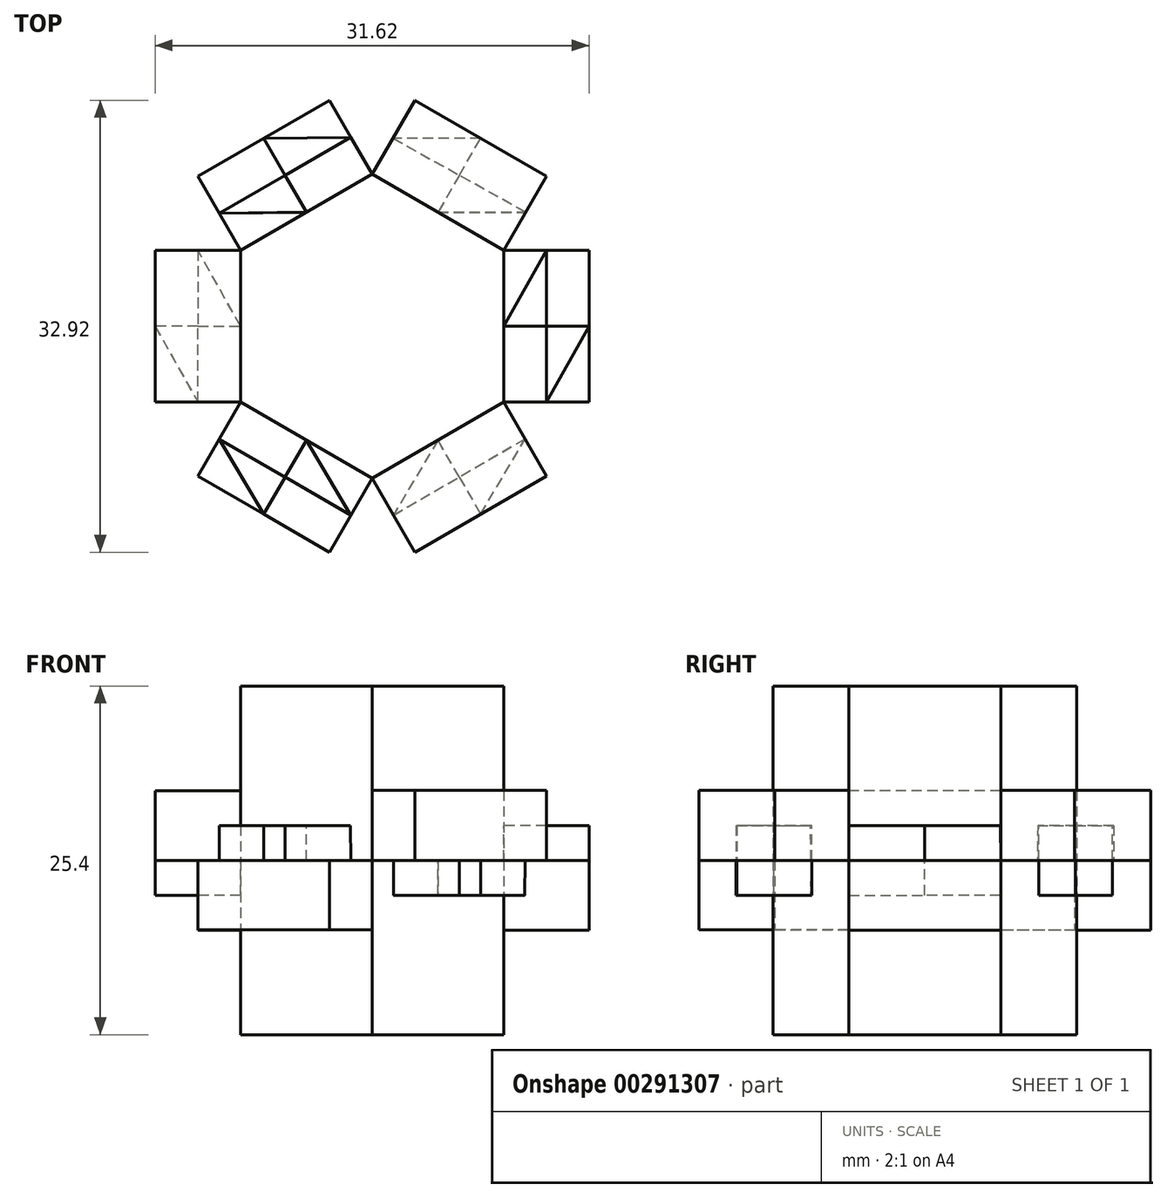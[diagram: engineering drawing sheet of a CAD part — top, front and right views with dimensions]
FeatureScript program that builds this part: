
annotation { "Feature Type Name" : "Feature", "Feature Type Description" : "" }
export const myFeature = defineFeature(function(context is Context, id is Id, definition is map)
    precondition{}
    {
        {
            var Q0;
            Q0=qCreatedBy(makeId("Top.planeOp"),FACE);
            var sketch = newSketch(context, id + "F0", { "sketchPlane" : qUnion([Q0])});
            skCircle(sketch, "E0.cCircle", {"center": v(0, 0) * mm, "radius": 11.07 * mm, "construction": true});
            skLineSegment(sketch, "E0.0", {"start": v(0, 11.07) * mm, "end": v(9.59, 5.53) * mm});
            skLineSegment(sketch, "E0.1", {"start": v(9.59, 5.53) * mm, "end": v(9.59, -5.53) * mm});
            skLineSegment(sketch, "E0.2", {"start": v(9.59, -5.53) * mm, "end": v(0, -11.07) * mm});
            skLineSegment(sketch, "E0.3", {"start": v(0, -11.07) * mm, "end": v(-9.59, -5.53) * mm});
            skLineSegment(sketch, "E0.4", {"start": v(-9.59, -5.53) * mm, "end": v(-9.59, 5.53) * mm});
            skLineSegment(sketch, "E0.5", {"start": v(-9.59, 5.53) * mm, "end": v(0, 11.07) * mm});
            skSolve(sketch);
        }
        {
            var Q0;
            Q0 = qSketchRegion(id + "F0", true);
            extrude(context, id + "F1", {"entities" : qUnion([Q0]), "endBound" : BoundingType.SYMMETRIC, "depth" : 25.4 * mm});
        }
        {
            var Q0;
            Q0=makeQuery(id+"F1.opExtrude","SWEPT_FACE",FACE,{"disambiguationData":[OSD([sQuery(id+"F0.wireOp",EDGE,"E0.4")])]});
            var sketch = newSketch(context, id + "F2", { "sketchPlane" : qUnion([Q0])});
            skLineSegment(sketch, "E1.bottom", {"start": v(-5.53, 0) * mm, "end": v(5.53, 0) * mm});
            skLineSegment(sketch, "E1.top", {"start": v(-5.53, 5.07) * mm, "end": v(5.53, 5.07) * mm});
            skLineSegment(sketch, "E1.left", {"start": v(-5.53, 0) * mm, "end": v(-5.53, 5.07) * mm});
            skLineSegment(sketch, "E1.right", {"start": v(5.53, 0) * mm, "end": v(5.53, 5.07) * mm});
            skSolve(sketch);
        }
        {
            var Q0;
            Q0=makeQuery(id+"F2.imprint","IMPRINT",FACE,{"disambiguationData":[TD([[makeQuery(id+"F2.imprint","IMPRINT",EDGE,{"derivedFrom":sQuery(id+"F2.wireOp",EDGE,"E1.bottom")}),1.0]])]});
            extrude(context, id + "F3", {"entities" : qUnion([Q0]), "operationType" : NewBodyOperationType.ADD, "depth" : 6.22 * mm});
        }
        {
            var Q0;
            Q0=makeQuery(id+"F3.opExtrude","SWEPT_FACE",FACE,{"disambiguationData":[OSD([sQuery(id+"F2.wireOp",EDGE,"E1.bottom")])]});
            var sketch = newSketch(context, id + "F4", { "sketchPlane" : qUnion([Q0])});
            skLineSegment(sketch, "E2", {"start": v(-15.8, 0) * mm, "end": v(-9.59, 0) * mm});
            skLineSegment(sketch, "E3", {"start": v(-9.59, 0) * mm, "end": v(-12.7, -5.53) * mm});
            skLineSegment(sketch, "E4", {"start": v(-12.7, -5.53) * mm, "end": v(-12.7, 5.53) * mm});
            skLineSegment(sketch, "E5", {"start": v(-12.7, 5.53) * mm, "end": v(-15.8, 0) * mm});
            skLineSegment(sketch, "E6", {"start": v(-12.7, -5.53) * mm, "end": v(-15.8, 0) * mm});
            skLineSegment(sketch, "E7", {"start": v(-12.7, 5.53) * mm, "end": v(-9.59, 0) * mm});
            skSolve(sketch);
        }
        {
            var Q0;
            {var subQ0=sQuery(id+"F4.wireOp",EDGE,"E5");Q0=makeQuery(id+"F4.imprint","IMPRINT",FACE,{"disambiguationData":[TD([[makeQuery(id+"F4.imprint","IMPRINT",EDGE,{"derivedFrom":subQ0}),1.0]])]});}
            var Q1;
            {var subQ0=sQuery(id+"F4.wireOp",EDGE,"E3");Q1=makeQuery(id+"F4.imprint","IMPRINT",FACE,{"disambiguationData":[TD([[makeQuery(id+"F4.imprint","IMPRINT",EDGE,{"derivedFrom":subQ0}),-1.0]])]});}
            var Q2;
            Q2=sQuery(id+"F4.wireOp",EDGE,"E5");
            extrude(context, id + "F5", {"entities" : qUnion([Q0, Q1]), "operationType" : NewBodyOperationType.ADD, "surfaceEntities" : qUnion([Q2]), "depth" : 2.54 * mm, "hasDraft" : true, "draftAngle" : .1 * degree, "draftPullDirection" : true});
        }
        {
            var Q0;
            Q0=makeQuery(id+"F1.opExtrude","SWEPT_FACE",FACE,{"disambiguationData":[OSD([sQuery(id+"F0.wireOp",EDGE,"E0.2")])]});
            var sketch = newSketch(context, id + "F6", { "sketchPlane" : qUnion([Q0])});
            skLineSegment(sketch, "E8.bottom", {"start": v(-5.53, 0) * mm, "end": v(5.53, 0) * mm});
            skLineSegment(sketch, "E8.top", {"start": v(-5.53, 5.08) * mm, "end": v(5.53, 5.08) * mm});
            skLineSegment(sketch, "E8.left", {"start": v(-5.53, 0) * mm, "end": v(-5.53, 5.08) * mm});
            skLineSegment(sketch, "E8.right", {"start": v(5.53, 0) * mm, "end": v(5.53, 5.08) * mm});
            skSolve(sketch);
        }
        {
            var Q0;
            Q0 = qSketchRegion(id + "F6", true);
            extrude(context, id + "F7", {"entities" : qUnion([Q0]), "operationType" : NewBodyOperationType.ADD, "depth" : 6.22 * mm});
        }
        {
            var Q0;
            Q0=makeQuery(id+"F7.opExtrude","SWEPT_FACE",FACE,{"disambiguationData":[OSD([sQuery(id+"F6.wireOp",EDGE,"E8.bottom")])]});
            var sketch = newSketch(context, id + "F8", { "sketchPlane" : qUnion([Q0])});
            skLineSegment(sketch, "E9", {"start": v(7.9, 13.7) * mm, "end": v(11.14, 8.23) * mm});
            skLineSegment(sketch, "E10", {"start": v(11.14, 8.23) * mm, "end": v(4.8, 8.3) * mm});
            skLineSegment(sketch, "E11", {"start": v(4.8, 8.3) * mm, "end": v(1.56, 13.76) * mm});
            skLineSegment(sketch, "E12", {"start": v(1.56, 13.76) * mm, "end": v(7.9, 13.7) * mm});
            skLineSegment(sketch, "E13", {"start": v(4.8, 8.3) * mm, "end": v(7.9, 13.7) * mm});
            skLineSegment(sketch, "E14", {"start": v(11.14, 8.23) * mm, "end": v(1.56, 13.76) * mm});
            skSolve(sketch);
        }
        {
            var Q0;
            {var subQ0=sQuery(id+"F8.wireOp",EDGE,"E11");Q0=makeQuery(id+"F8.imprint","IMPRINT",FACE,{"disambiguationData":[TD([[makeQuery(id+"F8.imprint","IMPRINT",EDGE,{"derivedFrom":subQ0}),-1.0]])]});}
            var Q1;
            {var subQ0=sQuery(id+"F8.wireOp",EDGE,"E9");Q1=makeQuery(id+"F8.imprint","IMPRINT",FACE,{"disambiguationData":[TD([[makeQuery(id+"F8.imprint","IMPRINT",EDGE,{"derivedFrom":subQ0}),-1.0]])]});}
            extrude(context, id + "F9", {"entities" : qUnion([Q0, Q1]), "operationType" : NewBodyOperationType.ADD, "depth" : 2.54 * mm, "hasDraft" : true, "draftAngle" : .1 * degree, "draftPullDirection" : true});
        }
        {
            var Q0;
            Q0=makeQuery(id+"F1.opExtrude","SWEPT_FACE",FACE,{"disambiguationData":[OSD([sQuery(id+"F0.wireOp",EDGE,"E0.0")])]});
            var sketch = newSketch(context, id + "F10", { "sketchPlane" : qUnion([Q0])});
            skLineSegment(sketch, "E15.bottom", {"start": v(5.53, 0) * mm, "end": v(-5.53, 0) * mm});
            skLineSegment(sketch, "E15.top", {"start": v(5.53, 5.09) * mm, "end": v(-5.53, 5.09) * mm});
            skLineSegment(sketch, "E15.left", {"start": v(5.53, 0) * mm, "end": v(5.53, 5.09) * mm});
            skLineSegment(sketch, "E15.right", {"start": v(-5.53, 0) * mm, "end": v(-5.53, 5.09) * mm});
            skSolve(sketch);
        }
        {
            var Q0;
            Q0=makeQuery(id+"F10.imprint","IMPRINT",FACE,{"disambiguationData":[TD([[makeQuery(id+"F10.imprint","IMPRINT",EDGE,{"derivedFrom":sQuery(id+"F10.wireOp",EDGE,"E15.bottom")}),-1.0]])]});
            extrude(context, id + "F11", {"entities" : qUnion([Q0]), "operationType" : NewBodyOperationType.ADD, "depth" : 6.22 * mm});
        }
        {
            var Q0;
            Q0=makeQuery(id+"F11.opExtrude","SWEPT_FACE",FACE,{"disambiguationData":[OSD([sQuery(id+"F10.wireOp",EDGE,"E15.bottom")])]});
            var sketch = newSketch(context, id + "F12", { "sketchPlane" : qUnion([Q0])});
            skLineSegment(sketch, "E16", {"start": v(4.8, -8.3) * mm, "end": v(11.18, -8.3) * mm});
            skLineSegment(sketch, "E17", {"start": v(11.18, -8.3) * mm, "end": v(7.9, -13.7) * mm});
            skLineSegment(sketch, "E18", {"start": v(7.9, -13.7) * mm, "end": v(1.51, -13.7) * mm});
            skLineSegment(sketch, "E19", {"start": v(1.51, -13.7) * mm, "end": v(4.8, -8.3) * mm});
            skLineSegment(sketch, "E20", {"start": v(7.9, -13.7) * mm, "end": v(4.8, -8.3) * mm});
            skLineSegment(sketch, "E21", {"start": v(11.18, -8.3) * mm, "end": v(1.51, -13.7) * mm});
            skSolve(sketch);
        }
        {
            var Q0;
            {var subQ0=sQuery(id+"F12.wireOp",EDGE,"E16");Q0=makeQuery(id+"F12.imprint","IMPRINT",FACE,{"disambiguationData":[TD([[makeQuery(id+"F12.imprint","IMPRINT",EDGE,{"derivedFrom":subQ0}),-1.0]])]});}
            var Q1;
            {var subQ0=sQuery(id+"F12.wireOp",EDGE,"E18");Q1=makeQuery(id+"F12.imprint","IMPRINT",FACE,{"disambiguationData":[TD([[makeQuery(id+"F12.imprint","IMPRINT",EDGE,{"derivedFrom":subQ0}),-1.0]])]});}
            extrude(context, id + "F13", {"entities" : qUnion([Q0, Q1]), "operationType" : NewBodyOperationType.ADD, "depth" : 2.54 * mm, "hasDraft" : true, "draftAngle" : .1 * degree, "draftPullDirection" : true});
        }
        {
            var Q0;
            Q0=makeQuery(id+"F1.opExtrude","SWEPT_FACE",FACE,{"disambiguationData":[OSD([sQuery(id+"F0.wireOp",EDGE,"E0.1")])]});
            var sketch = newSketch(context, id + "F14", { "sketchPlane" : qUnion([Q0])});
            skLineSegment(sketch, "E22.bottom", {"start": v(-5.53, 0) * mm, "end": v(5.53, 0) * mm});
            skLineSegment(sketch, "E22.top", {"start": v(-5.53, -5.1) * mm, "end": v(5.53, -5.1) * mm});
            skLineSegment(sketch, "E22.left", {"start": v(-5.53, 0) * mm, "end": v(-5.53, -5.1) * mm});
            skLineSegment(sketch, "E22.right", {"start": v(5.53, 0) * mm, "end": v(5.53, -5.1) * mm});
            skSolve(sketch);
        }
        {
            var Q0;
            Q0=makeQuery(id+"F14.imprint","IMPRINT",FACE,{"disambiguationData":[TD([[makeQuery(id+"F14.imprint","IMPRINT",EDGE,{"derivedFrom":sQuery(id+"F14.wireOp",EDGE,"E22.bottom")}),-1.0]])]});
            extrude(context, id + "F15", {"entities" : qUnion([Q0]), "operationType" : NewBodyOperationType.ADD, "depth" : 6.22 * mm});
        }
        {
            var Q0;
            Q0=makeQuery(id+"F15.opExtrude","SWEPT_FACE",FACE,{"disambiguationData":[OSD([sQuery(id+"F14.wireOp",EDGE,"E22.bottom")])]});
            var sketch = newSketch(context, id + "F16", { "sketchPlane" : qUnion([Q0])});
            skLineSegment(sketch, "E23", {"start": v(15.8, 0) * mm, "end": v(9.59, 0) * mm});
            skLineSegment(sketch, "E24", {"start": v(9.59, 0) * mm, "end": v(12.7, -5.53) * mm});
            skLineSegment(sketch, "E25", {"start": v(12.7, -5.53) * mm, "end": v(12.7, 5.53) * mm});
            skLineSegment(sketch, "E26", {"start": v(12.7, 5.53) * mm, "end": v(15.8, 0) * mm});
            skLineSegment(sketch, "E27", {"start": v(15.8, 0) * mm, "end": v(12.7, -5.53) * mm});
            skLineSegment(sketch, "E28", {"start": v(12.7, 5.53) * mm, "end": v(9.59, 0) * mm});
            skSolve(sketch);
        }
        {
            var Q0;
            {var subQ0=sQuery(id+"F16.wireOp",EDGE,"E28");Q0=makeQuery(id+"F16.imprint","IMPRINT",FACE,{"disambiguationData":[TD([[makeQuery(id+"F16.imprint","IMPRINT",EDGE,{"derivedFrom":subQ0}),1.0]])]});}
            var Q1;
            {var subQ0=sQuery(id+"F16.wireOp",EDGE,"E27");Q1=makeQuery(id+"F16.imprint","IMPRINT",FACE,{"disambiguationData":[TD([[makeQuery(id+"F16.imprint","IMPRINT",EDGE,{"derivedFrom":subQ0}),-1.0]])]});}
            extrude(context, id + "F17", {"entities" : qUnion([Q0, Q1]), "operationType" : NewBodyOperationType.ADD, "depth" : 2.54 * mm, "hasDraft" : true, "draftAngle" : .1 * degree, "draftPullDirection" : true});
        }
        {
            var Q0;
            Q0=makeQuery(id+"F1.opExtrude","SWEPT_FACE",FACE,{"disambiguationData":[OSD([sQuery(id+"F0.wireOp",EDGE,"E0.5")])]});
            var sketch = newSketch(context, id + "F18", { "sketchPlane" : qUnion([Q0])});
            skLineSegment(sketch, "E29.bottom", {"start": v(-5.53, 0) * mm, "end": v(5.53, 0) * mm});
            skLineSegment(sketch, "E29.top", {"start": v(-5.53, -5.09) * mm, "end": v(5.53, -5.09) * mm});
            skLineSegment(sketch, "E29.left", {"start": v(-5.53, 0) * mm, "end": v(-5.53, -5.09) * mm});
            skLineSegment(sketch, "E29.right", {"start": v(5.53, 0) * mm, "end": v(5.53, -5.09) * mm});
            skSolve(sketch);
        }
        {
            var Q0;
            Q0=makeQuery(id+"F18.imprint","IMPRINT",FACE,{"disambiguationData":[TD([[makeQuery(id+"F18.imprint","IMPRINT",EDGE,{"derivedFrom":sQuery(id+"F18.wireOp",EDGE,"E29.bottom")}),-1.0]])]});
            extrude(context, id + "F19", {"entities" : qUnion([Q0]), "operationType" : NewBodyOperationType.ADD, "depth" : 6.22 * mm});
        }
        {
            var Q0;
            Q0=makeQuery(id+"F19.opExtrude","SWEPT_FACE",FACE,{"disambiguationData":[OSD([sQuery(id+"F18.wireOp",EDGE,"E29.bottom")])]});
            var sketch = newSketch(context, id + "F20", { "sketchPlane" : qUnion([Q0])});
            skLineSegment(sketch, "E30", {"start": v(-1.56, 13.76) * mm, "end": v(-4.8, 8.3) * mm});
            skLineSegment(sketch, "E31", {"start": v(-4.8, 8.3) * mm, "end": v(-7.9, 13.7) * mm});
            skLineSegment(sketch, "E32", {"start": v(-7.9, 13.7) * mm, "end": v(-11.14, 8.23) * mm});
            skLineSegment(sketch, "E33", {"start": v(-11.14, 8.23) * mm, "end": v(-1.56, 13.76) * mm});
            skLineSegment(sketch, "E34", {"start": v(-1.56, 13.76) * mm, "end": v(-7.9, 13.7) * mm});
            skLineSegment(sketch, "E35", {"start": v(-4.8, 8.3) * mm, "end": v(-11.14, 8.23) * mm});
            skSolve(sketch);
        }
        {
            var Q0;
            {var subQ0=sQuery(id+"F20.wireOp",EDGE,"E34");Q0=makeQuery(id+"F20.imprint","IMPRINT",FACE,{"disambiguationData":[TD([[makeQuery(id+"F20.imprint","IMPRINT",EDGE,{"derivedFrom":subQ0}),1.0]])]});}
            var Q1;
            {var subQ0=sQuery(id+"F20.wireOp",EDGE,"E35");Q1=makeQuery(id+"F20.imprint","IMPRINT",FACE,{"disambiguationData":[TD([[makeQuery(id+"F20.imprint","IMPRINT",EDGE,{"derivedFrom":subQ0}),-1.0]])]});}
            extrude(context, id + "F21", {"entities" : qUnion([Q0, Q1]), "operationType" : NewBodyOperationType.ADD, "depth" : 2.54 * mm, "hasDraft" : true, "draftAngle" : .1 * degree, "draftPullDirection" : true});
        }
        {
            var Q0;
            Q0=makeQuery(id+"F1.opExtrude","SWEPT_FACE",FACE,{"disambiguationData":[OSD([sQuery(id+"F0.wireOp",EDGE,"E0.3")])]});
            var sketch = newSketch(context, id + "F22", { "sketchPlane" : qUnion([Q0])});
            skLineSegment(sketch, "E36.bottom", {"start": v(-5.53, 0) * mm, "end": v(5.53, 0) * mm});
            skLineSegment(sketch, "E36.top", {"start": v(-5.53, -5.07) * mm, "end": v(5.53, -5.07) * mm});
            skLineSegment(sketch, "E36.left", {"start": v(-5.53, 0) * mm, "end": v(-5.53, -5.07) * mm});
            skLineSegment(sketch, "E36.right", {"start": v(5.53, 0) * mm, "end": v(5.53, -5.07) * mm});
            skSolve(sketch);
        }
        {
            var Q0;
            Q0=makeQuery(id+"F22.imprint","IMPRINT",FACE,{"disambiguationData":[TD([[makeQuery(id+"F22.imprint","IMPRINT",EDGE,{"derivedFrom":sQuery(id+"F22.wireOp",EDGE,"E36.bottom")}),-1.0]])]});
            extrude(context, id + "F23", {"entities" : qUnion([Q0]), "operationType" : NewBodyOperationType.ADD, "depth" : 6.22 * mm});
        }
        {
            var Q0;
            Q0=makeQuery(id+"F23.opExtrude","SWEPT_FACE",FACE,{"disambiguationData":[OSD([sQuery(id+"F22.wireOp",EDGE,"E36.bottom")])]});
            var sketch = newSketch(context, id + "F24", { "sketchPlane" : qUnion([Q0])});
            skLineSegment(sketch, "E37", {"start": v(-11.14, -8.23) * mm, "end": v(-7.9, -13.7) * mm});
            skLineSegment(sketch, "E38", {"start": v(-7.9, -13.7) * mm, "end": v(-1.56, -13.76) * mm});
            skLineSegment(sketch, "E39", {"start": v(-1.56, -13.76) * mm, "end": v(-4.8, -8.3) * mm});
            skLineSegment(sketch, "E40", {"start": v(-4.8, -8.3) * mm, "end": v(-11.14, -8.23) * mm});
            skLineSegment(sketch, "E41", {"start": v(-11.14, -8.23) * mm, "end": v(-1.56, -13.76) * mm});
            skLineSegment(sketch, "E42", {"start": v(-7.9, -13.7) * mm, "end": v(-4.8, -8.3) * mm});
            skSolve(sketch);
        }
        {
            var Q0;
            {var subQ0=sQuery(id+"F24.wireOp",EDGE,"E39");Q0=makeQuery(id+"F24.imprint","IMPRINT",FACE,{"disambiguationData":[TD([[makeQuery(id+"F24.imprint","IMPRINT",EDGE,{"derivedFrom":subQ0}),1.0]])]});}
            var Q1;
            {var subQ0=sQuery(id+"F24.wireOp",EDGE,"E37");Q1=makeQuery(id+"F24.imprint","IMPRINT",FACE,{"disambiguationData":[TD([[makeQuery(id+"F24.imprint","IMPRINT",EDGE,{"derivedFrom":subQ0}),1.0]])]});}
            extrude(context, id + "F25", {"entities" : qUnion([Q0, Q1]), "operationType" : NewBodyOperationType.ADD, "depth" : 2.54 * mm, "hasDraft" : true, "draftAngle" : .1 * degree, "draftPullDirection" : true});
        }
    });
